# Revit family: Loading-Dock-Equipment_Restraint_McGuire
name_source: partatom
category: Specialty Equipment
units: mm (PartAtom-declared; Revit-internal decimal feet)

## family parameters
Always vertical = No
Classification Number = 23.50.70.27
Cut with Voids When Loaded = No
Enable Cutting in Views = No
Maintain Annotation Orientation = No
Part Type = Normal
Room Calculation Point = No
Round Connector Dimension = Use Diameter
Shared = No
Work Plane-Based = Yes

## types (1)
- as Specified
    Arm Finish = Metal - McGuire - Arm Coating
    Assembly Code = E1030300
    Capacity = as Specified
    Default Elevation = 0' - 0"
    Description = McGuire Loading Dock Product as Specified
    Expected Lifespan (Years) = 0
    Green Building-LEED = http://www.arcat.com
    Keynote = 11160
    Maintenance Schedule (Months) = 0
    Manufacturer = McGuire
    Manufacturer Fax = 262-255-4199
    Manufacturer Website = http://www.wbmcguire.com
    Model = As Specified
    Panel Material = Metal - McGuire - Zinc Coated Steel
    Product Data = http://www.arcat.com
    Sales Information = http://www.wbmcguire.com
    Standard Hook = Yes
    Standards Conformance = as Specified
    URL = http://www.wbmcguire.com
    Unit Depth = 2' - 11"
    Unit Height = 1' - 4 3/8"
    Unit Width = 1' - 1"
    Warranty Duration (Years) = 0

## geometry (parser evidence)
native form markers: Blend x4, Sweep x1
no freeform markers — native parametric forms only
